# Revit family: BE_33158_de_DE
name_source: partatom
category: Leuchten
revit_build: Autodesk Revit 2015 (Build: 20150704_0715(x64)
units: mm (PartAtom-declared; Revit-internal decimal feet)

## types (4) — shared parameters
AC/DC = AC/DC
Aktualisierung = 2015-10-21T04:08:05
BEGA_Dummy = Nein
BEGA_IES = Ja
BEGA_Intern = Ja
BEGA_Intern_Konstruktion = Ja
BEGA_Intern_an = Ja
BEGA_Intern_aus = Ja
Beschreibung = Einbauleuchte
Beschreibung_Sonderanfertigung = Hier können Sie Informationen zur Sonderanfertigung eintragen.
Bestellnummer_Einbaugehäuse = ---
CE_Konformität = ja
Einbaugehäuse = Nein
Einbautiefe = 90 mm
Einbauöffnung = 505 x 110 mm
Energieeffizienzklasse = LED A++ - A
Farbfilter = 16777215
Farbtemperaturverschiebung bei Dämpfen der Lampe = <Keine Auswahl>
Farbwiedergabeindex = Ra > 80
Frequenz = 0/50-60 Hz
Hersteller = BEGA
Lampe = LED 10 W
Lampenlichtstrom = 1500 lm
Lastklassifizierung = Beleuchtung
Lebensdauerkriterien = L70 = 50.000 h
Leuchtenlichtstrom = 938 lm
Logo = BEGA_Logo.png
Material_02 = BEGA_Oberfläche_Silber_matt
Material_06 = BEGA_Oberfläche_Edelstahl_gebürstet
Material_11 = BEGA_Glas_opal
Neigungswinkel = 0.00°
Produktdatenblatt = http://www.bega.de
Scheinlast = 0 VA
Schutzart = IP 65
Schutzklasse = I
Sonderanfertigung = Nein
Spannung = 0 V
Typenbild = 33158.png
URL = http://www.bega.de
Umgebungstemperatur = 25 °C
zero-valued in all types: Vorgabe-Ansicht

## per-type parameters (varying)
| type | Bestellnummer | Datei für fotometrisches Netz | Farbtemperatur | LED_Modulbezeichnung | M_A | M_G | Modell |
| BEGA_33158_Grafit_K4 | 33158K4 | BE_33158K4.IES | 4000 K | LED-0568/840 | Nein | Ja | 33158K4 |
| BEGA_33158_Silber_K4 | 33158AK4 | BE_33158K4.IES | 4000 K | LED-0568/840 | Ja | Nein | 33158AK4 |
| BEGA_33158_Silber_K3 | 33158A | BE_33158.IES | 3000 K | LED-0568/830 | Ja | Nein | 33158A |
| BEGA_33158_Grafit_K3 | 33158 | BE_33158.IES | 3000 K | LED-0568/830 | Nein | Ja | 33158 |
